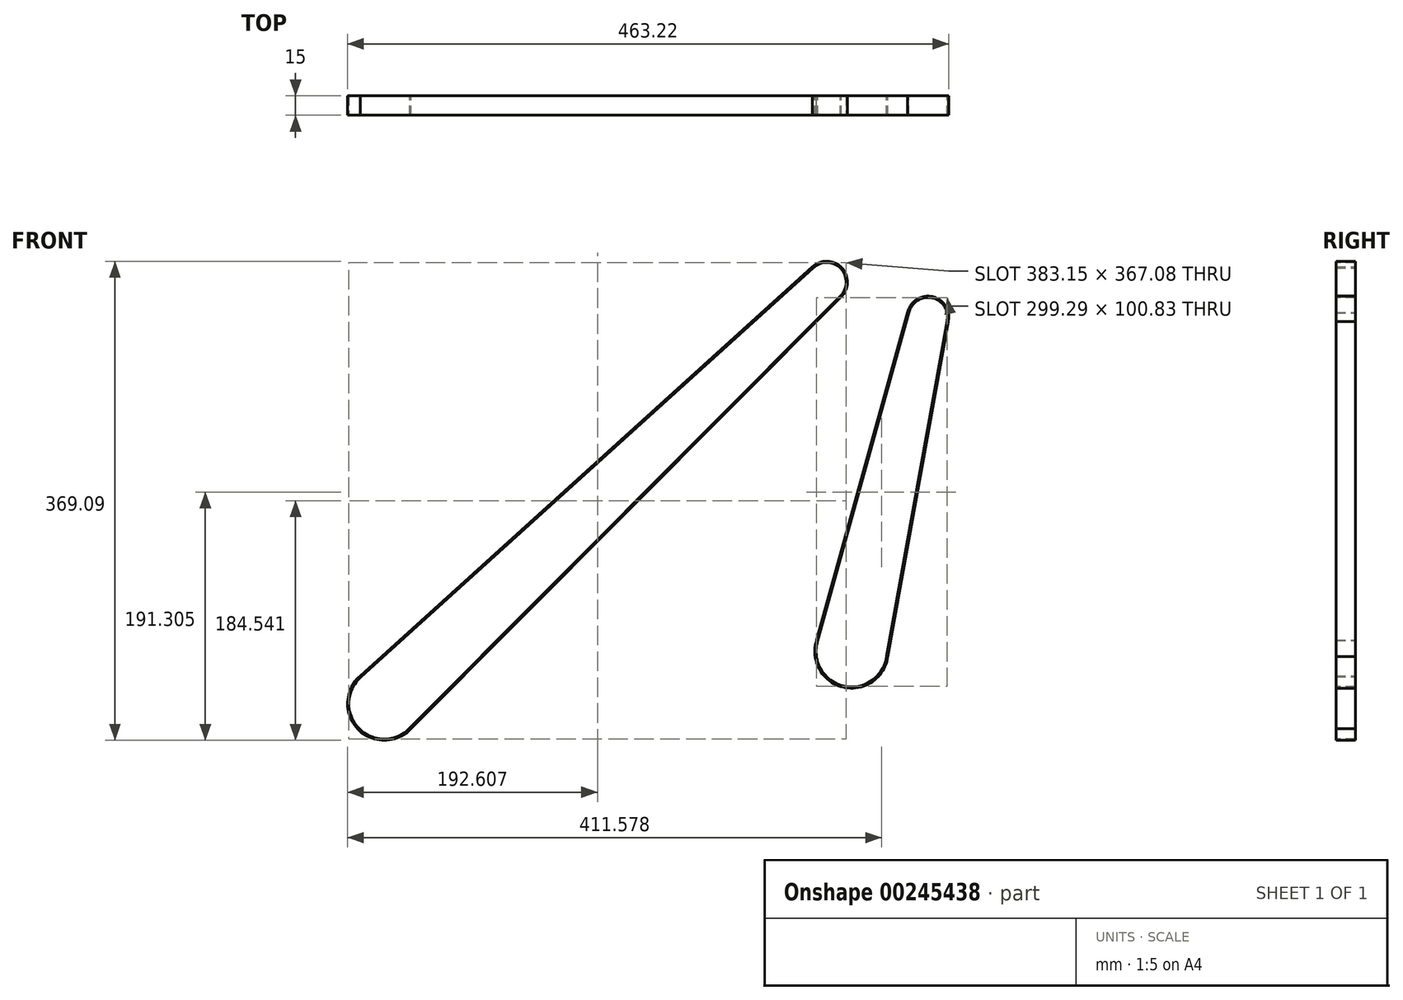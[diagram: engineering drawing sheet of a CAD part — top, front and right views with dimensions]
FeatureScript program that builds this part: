
annotation { "Feature Type Name" : "Feature", "Feature Type Description" : "" }
export const myFeature = defineFeature(function(context is Context, id is Id, definition is map)
    precondition{}
    {
        {
            var Q0;
            Q0=qCreatedBy(makeId("Front.planeOp"),FACE);
            var sketch = newSketch(context, id + "F0", { "sketchPlane" : qUnion([Q0])});
            skLineSegment(sketch, "E0", {"start": v(58.97, 477.94) * mm, "end": v(0.03, 220.17) * mm});
            skLineSegment(sketch, "E1", {"start": v(0, 0) * mm, "end": v(-360, 0) * mm});
            skLineSegment(sketch, "E2", {"start": v(-360, 0) * mm, "end": v(-360, 180) * mm});
            skLineSegment(sketch, "E3", {"start": v(-19.06, 504.84) * mm, "end": v(-360, 180) * mm});
            skLineSegment(sketch, "E4", {"start": v(-0.18, 567.04) * mm, "end": v(-219.82, 505.07) * mm});
            skLineSegment(sketch, "E5", {"start": v(-224.47, 531.92) * mm, "end": v(-4.17, 581.5) * mm});
            skLineSegment(sketch, "E6", {"start": v(-209.74, 479.75) * mm, "end": v(3.98, 552.63) * mm});
            skLineSegment(sketch, "E7", {"start": v(-340.2, 161.28) * mm, "end": v(-8.69, 494) * mm});
            skLineSegment(sketch, "E8", {"start": v(-377.78, 200.65) * mm, "end": v(-29.38, 515.73) * mm});
            skLineSegment(sketch, "E9", {"start": v(27.03, 216.5) * mm, "end": v(73.6, 474.67) * mm});
            skLineSegment(sketch, "E10", {"start": v(44.3, 481.04) * mm, "end": v(-25.89, 228.6) * mm});
            skLineSegment(sketch, "E11.0", {"start": v(-339.49, 160.58) * mm, "end": v(-7.99, 493.3) * mm});
            skArc(sketch, "E11.1", {"start": v(-378.44, 201.4) * mm, "mid": v(-380.44, 160.5) * mm, "end": v(-339.49, 160.58) * mm});
            skLineSegment(sketch, "E11.2", {"start": v(-378.44, 201.4) * mm, "end": v(-30.06, 516.46) * mm});
            skArc(sketch, "E11.3", {"start": v(-7.99, 493.3) * mm, "mid": v(-7.48, 515.87) * mm, "end": v(-30.06, 516.46) * mm});
            skLineSegment(sketch, "E12.0", {"start": v(-209.4, 478.81) * mm, "end": v(4.28, 551.68) * mm});
            skArc(sketch, "E12.1", {"start": v(-224.66, 532.9) * mm, "mid": v(-247, 497.4) * mm, "end": v(-209.4, 478.81) * mm});
            skLineSegment(sketch, "E12.2", {"start": v(-224.66, 532.9) * mm, "end": v(-4.41, 582.47) * mm});
            skArc(sketch, "E12.3", {"start": v(4.28, 551.68) * mm, "mid": v(15.22, 571.4) * mm, "end": v(-4.41, 582.47) * mm});
            skLineSegment(sketch, "E13.0", {"start": v(28.02, 216.34) * mm, "end": v(74.59, 474.47) * mm});
            skArc(sketch, "E13.1", {"start": v(-26.84, 228.89) * mm, "mid": v(-6.27, 192.63) * mm, "end": v(28.02, 216.34) * mm});
            skLineSegment(sketch, "E13.2", {"start": v(43.32, 481.28) * mm, "end": v(-26.84, 228.89) * mm});
            skArc(sketch, "E13.3", {"start": v(74.59, 474.47) * mm, "mid": v(62.37, 493.58) * mm, "end": v(43.32, 481.28) * mm});
            skArc(sketch, "E14", {"start": v(44.3, 481.04) * mm, "mid": v(55.78, 463.29) * mm, "end": v(73.6, 474.67) * mm});
            skArc(sketch, "E15", {"start": v(27.03, 216.5) * mm, "mid": v(6.1, 246.73) * mm, "end": v(-25.89, 228.6) * mm});
            skCircle(sketch, "E16", {"center": v(0.03, 220.17) * mm, "radius": 17.5 * mm});
            skCircle(sketch, "E17", {"center": v(58.97, 477.94) * mm, "radius": 3 * mm});
            skArc(sketch, "E18", {"start": v(-340.2, 161.28) * mm, "mid": v(-340.29, 198.81) * mm, "end": v(-377.78, 200.65) * mm});
            skCircle(sketch, "E19", {"center": v(-360, 180) * mm, "radius": 17.5 * mm});
            skArc(sketch, "E20", {"start": v(-29.38, 515.73) * mm, "mid": v(-29.92, 494.49) * mm, "end": v(-8.69, 494) * mm});
            skCircle(sketch, "E21", {"center": v(-19.06, 504.84) * mm, "radius": 3 * mm});
            skArc(sketch, "E22", {"start": v(-4.17, 581.5) * mm, "mid": v(-14.61, 562.97) * mm, "end": v(3.98, 552.63) * mm});
            skCircle(sketch, "E23", {"center": v(-0.18, 567.04) * mm, "radius": 3 * mm});
            skArc(sketch, "E24", {"start": v(-209.74, 479.75) * mm, "mid": v(-193.6, 512.47) * mm, "end": v(-224.47, 531.92) * mm});
            skCircle(sketch, "E25", {"center": v(-219.82, 505.07) * mm, "radius": 17.5 * mm});
            skSolve(sketch);
        }
        {
            var Q0;
            Q0=qSketchRegion(id+"F0",true);
            extrude(context, id + "F1", {"entities" : qUnion([Q0]), "depth" : 15 * mm});
        }
        {
            var Q0;
            Q0=makeQuery(id+"F1.opExtrude","CAP_FACE",FACE,{"disambiguationData":[OSD([sQuery(id+"F0.wireOp",EDGE,"E9"),sQuery(id+"F0.wireOp",EDGE,"E10"),sQuery(id+"F0.wireOp",EDGE,"E13.0"),sQuery(id+"F0.wireOp",EDGE,"E13.1"),sQuery(id+"F0.wireOp",EDGE,"E13.2"),sQuery(id+"F0.wireOp",EDGE,"E13.3"),sQuery(id+"F0.wireOp",EDGE,"E14"),sQuery(id+"F0.wireOp",EDGE,"E15"),sQuery(id+"F0.wireOp",EDGE,"E16"),sQuery(id+"F0.wireOp",EDGE,"E17")])],"isStart":false});
            var sketch = newSketch(context, id + "F2", { "sketchPlane" : qUnion([Q0])});
            skCircle(sketch, "E26", {"center": v(58.97, 477.94) * mm, "radius": 8 * mm});
            skCircle(sketch, "E27", {"center": v(58.97, 477.94) * mm, "radius": 3 * mm});
            skSolve(sketch);
        }
        {
            var Q0;
            Q0=qSketchRegion(id+"F2",true);
            extrude(context, id + "F3", {"entities" : qUnion([Q0]), "operationType" : NewBodyOperationType.ADD, "depth" : 10 * mm});
        }
        {
            var Q0;
            Q0=makeQuery(id+"F1.opExtrude","CAP_FACE",FACE,{"disambiguationData":[OSD([sQuery(id+"F0.wireOp",EDGE,"E7"),sQuery(id+"F0.wireOp",EDGE,"E8"),sQuery(id+"F0.wireOp",EDGE,"E11.0"),sQuery(id+"F0.wireOp",EDGE,"E11.1"),sQuery(id+"F0.wireOp",EDGE,"E11.2"),sQuery(id+"F0.wireOp",EDGE,"E11.3"),sQuery(id+"F0.wireOp",EDGE,"E18"),sQuery(id+"F0.wireOp",EDGE,"E19"),sQuery(id+"F0.wireOp",EDGE,"E20"),sQuery(id+"F0.wireOp",EDGE,"E21")])],"isStart":false});
            var sketch = newSketch(context, id + "F4", { "sketchPlane" : qUnion([Q0])});
            skCircle(sketch, "E28", {"center": v(-19.06, 504.84) * mm, "radius": 3 * mm});
            skCircle(sketch, "E29", {"center": v(-19.06, 504.84) * mm, "radius": 8 * mm});
            skSolve(sketch);
        }
        {
            var Q0;
            Q0=qSketchRegion(id+"F4",true);
            extrude(context, id + "F5", {"entities" : qUnion([Q0]), "operationType" : NewBodyOperationType.ADD, "depth" : 10 * mm});
        }
        {
            var Q0;
            Q0=makeQuery(id+"F1.opExtrude","CAP_FACE",FACE,{"disambiguationData":[OSD([sQuery(id+"F0.wireOp",EDGE,"E5"),sQuery(id+"F0.wireOp",EDGE,"E6"),sQuery(id+"F0.wireOp",EDGE,"E12.0"),sQuery(id+"F0.wireOp",EDGE,"E12.1"),sQuery(id+"F0.wireOp",EDGE,"E12.2"),sQuery(id+"F0.wireOp",EDGE,"E12.3"),sQuery(id+"F0.wireOp",EDGE,"E22"),sQuery(id+"F0.wireOp",EDGE,"E23"),sQuery(id+"F0.wireOp",EDGE,"E24"),sQuery(id+"F0.wireOp",EDGE,"E25")])],"isStart":false});
            var sketch = newSketch(context, id + "F6", { "sketchPlane" : qUnion([Q0])});
            skCircle(sketch, "E30", {"center": v(-0.18, 567.04) * mm, "radius": 3 * mm});
            skCircle(sketch, "E31", {"center": v(-0.18, 567.04) * mm, "radius": 8 * mm});
            skSolve(sketch);
        }
        {
            var Q0;
            Q0=qSketchRegion(id+"F6",true);
            extrude(context, id + "F7", {"entities" : qUnion([Q0]), "operationType" : NewBodyOperationType.ADD, "depth" : 10 * mm});
        }
        {
            var Q0;
            Q0=makeQuery(id+"F1.opExtrude","CAP_FACE",FACE,{"disambiguationData":[OSD([sQuery(id+"F0.wireOp",EDGE,"E9"),sQuery(id+"F0.wireOp",EDGE,"E10"),sQuery(id+"F0.wireOp",EDGE,"E13.0"),sQuery(id+"F0.wireOp",EDGE,"E13.1"),sQuery(id+"F0.wireOp",EDGE,"E13.2"),sQuery(id+"F0.wireOp",EDGE,"E13.3"),sQuery(id+"F0.wireOp",EDGE,"E14"),sQuery(id+"F0.wireOp",EDGE,"E15"),sQuery(id+"F0.wireOp",EDGE,"E16"),sQuery(id+"F0.wireOp",EDGE,"E17")])],"isStart":false});
            var sketch = newSketch(context, id + "F8", { "sketchPlane" : qUnion([Q0])});
            skCircle(sketch, "E32", {"center": v(0.03, 220.17) * mm, "radius": 27.25 * mm});
            skCircle(sketch, "E33", {"center": v(58.97, 477.94) * mm, "radius": 15 * mm});
            skSolve(sketch);
        }
        {
            var Q0;
            Q0 = qSketchRegion(id + "F8", true);
            extrude(context, id + "F9", {"entities" : qUnion([Q0]), "operationType" : NewBodyOperationType.REMOVE, "endBound" : BoundingType.SYMMETRIC, "oppositeDirection" : true, "depth" : 40 * mm, "offsetDistance" : 25 * mm});
        }
        {
            var Q0;
            Q0=makeQuery(id+"F1.opExtrude","SWEPT_BODY",BODY,{"disambiguationData":[OSD([sQuery(id+"F0.wireOp",EDGE,"E5"),sQuery(id+"F0.wireOp",EDGE,"E6"),sQuery(id+"F0.wireOp",EDGE,"E12.0"),sQuery(id+"F0.wireOp",EDGE,"E12.1"),sQuery(id+"F0.wireOp",EDGE,"E12.2"),sQuery(id+"F0.wireOp",EDGE,"E12.3"),sQuery(id+"F0.wireOp",EDGE,"E22"),sQuery(id+"F0.wireOp",EDGE,"E23"),sQuery(id+"F0.wireOp",EDGE,"E24"),sQuery(id+"F0.wireOp",EDGE,"E25")])]});
            deleteBodies(context, id + "F10", {"entities" : qUnion([Q0])});
        }
        {
            var Q0;
            Q0=makeQuery(id+"F1.opExtrude","CAP_FACE",FACE,{"disambiguationData":[OSD([sQuery(id+"F0.wireOp",EDGE,"E7"),sQuery(id+"F0.wireOp",EDGE,"E8"),sQuery(id+"F0.wireOp",EDGE,"E11.0"),sQuery(id+"F0.wireOp",EDGE,"E11.1"),sQuery(id+"F0.wireOp",EDGE,"E11.2"),sQuery(id+"F0.wireOp",EDGE,"E11.3"),sQuery(id+"F0.wireOp",EDGE,"E18"),sQuery(id+"F0.wireOp",EDGE,"E19"),sQuery(id+"F0.wireOp",EDGE,"E20"),sQuery(id+"F0.wireOp",EDGE,"E21")])],"isStart":false});
            var sketch = newSketch(context, id + "F11", { "sketchPlane" : qUnion([Q0])});
            skCircle(sketch, "E34", {"center": v(-19.06, 504.84) * mm, "radius": 15 * mm});
            skCircle(sketch, "E35", {"center": v(-360, 180) * mm, "radius": 27.25 * mm});
            skSolve(sketch);
        }
        {
            var Q0;
            Q0 = qSketchRegion(id + "F11", true);
            extrude(context, id + "F12", {"entities" : qUnion([Q0]), "operationType" : NewBodyOperationType.REMOVE, "endBound" : BoundingType.SYMMETRIC, "oppositeDirection" : true, "depth" : 40 * mm, "offsetDistance" : 25 * mm});
        }
    });
